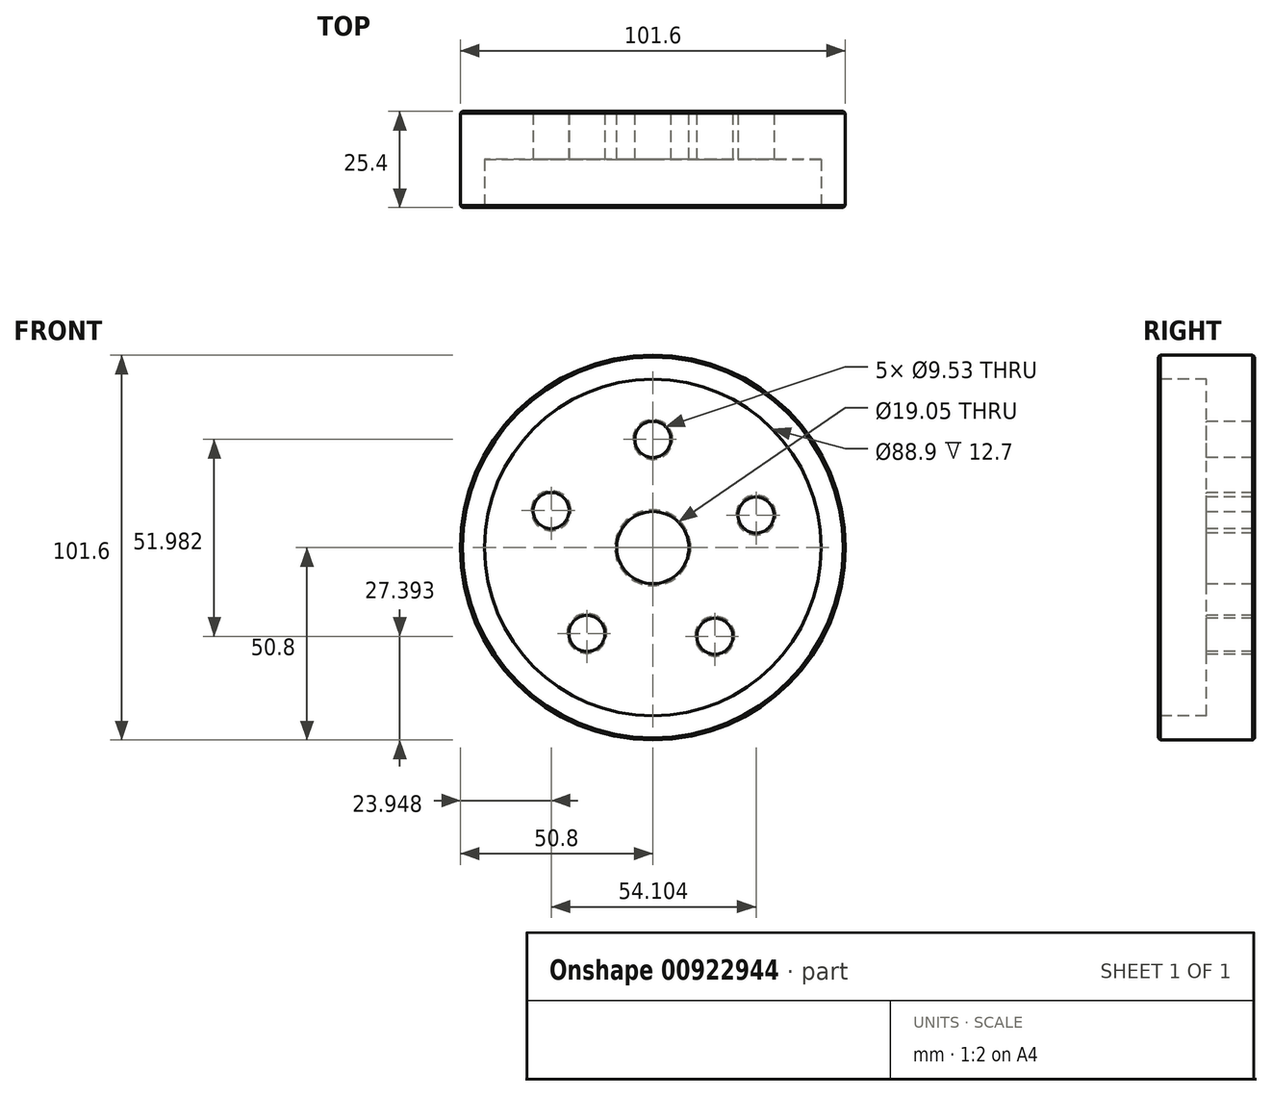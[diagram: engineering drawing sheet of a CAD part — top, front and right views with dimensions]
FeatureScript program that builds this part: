
annotation { "Feature Type Name" : "Feature", "Feature Type Description" : "" }
export const myFeature = defineFeature(function(context is Context, id is Id, definition is map)
    precondition{}
    {
        {
            var Q0;
            Q0=qCreatedBy(makeId("Front.planeOp"),FACE);
            var sketch = newSketch(context, id + "F0", { "sketchPlane" : qUnion([Q0])});
            skCircle(sketch, "E0", {"center": v(0, 0) * mm, "radius": 50.8 * mm});
            skCircle(sketch, "E1", {"center": v(0, 0) * mm, "radius": 9.53 * mm});
            skSolve(sketch);
        }
        {
            var Q0;
            Q0=makeQuery(id+"F0.imprint","IMPRINT",FACE,{"disambiguationData":[TD([[makeQuery(id+"F0.imprint","IMPRINT",EDGE,{"derivedFrom":sQuery(id+"F0.wireOp",EDGE,"E0")}),1.0]])]});
            extrude(context, id + "F1", {"entities" : qUnion([Q0]), "depth" : 25.4 * mm, "offsetDistance" : 25.4 * mm});
        }
        {
            var Q0;
            Q0=makeQuery(id+"F1.opExtrude","CAP_FACE",FACE,{"disambiguationData":[OSD([sQuery(id+"F0.wireOp",EDGE,"E0"),sQuery(id+"F0.wireOp",EDGE,"E1")])],"isStart":false});
            var sketch = newSketch(context, id + "F2", { "sketchPlane" : qUnion([Q0])});
            skCircle(sketch, "E2", {"center": v(0, 0) * mm, "radius": 44.45 * mm});
            skSolve(sketch);
        }
        {
            var Q0;
            Q0=makeQuery(id+"F2.imprint","IMPRINT",FACE,{"disambiguationData":[TD([[makeQuery(id+"F2.imprint","IMPRINT",EDGE,{"derivedFrom":sQuery(id+"F2.wireOp",EDGE,"E2")}),1.0]])]});
            extrude(context, id + "F3", {"entities" : qUnion([Q0]), "operationType" : NewBodyOperationType.REMOVE, "oppositeDirection" : true, "depth" : 12.7 * mm, "offsetDistance" : 25.4 * mm});
        }
        {
            var Q0;
            Q0=makeQuery(id+"F3.boolean.opBoolean","COPY",FACE,{"derivedFrom":makeQuery(id+"F3.opExtrude","CAP_FACE",FACE,{"disambiguationData":[OSD([sQuery(id+"F0.wireOp",EDGE,"E1"),sQuery(id+"F2.wireOp",EDGE,"E2")])],"isStart":false})});
            var sketch = newSketch(context, id + "F4", { "sketchPlane" : qUnion([Q0])});
            skCircle(sketch, "E3", {"center": v(0, 28.58) * mm, "radius": 4.76 * mm});
            skCircle(sketch, "E4.1.0", {"center": v(27.25, 8.6) * mm, "radius": 4.76 * mm});
            skCircle(sketch, "E4.2.0", {"center": v(16.39, -23.4) * mm, "radius": 4.76 * mm});
            skCircle(sketch, "E4.3.0", {"center": v(-17.4, -22.67) * mm, "radius": 4.76 * mm});
            skCircle(sketch, "E4.4.0", {"center": v(-26.85, 9.77) * mm, "radius": 4.76 * mm});
            skPoint(sketch, "E4.center", {"position": v(0, 0) * mm});
            skLineSegment(sketch, "E4.anchor1", {"start": v(0, 0) * mm, "end": v(0, 28.58) * mm, "construction": true});
            skLineSegment(sketch, "E4.anchor2", {"start": v(0, 0) * mm, "end": v(-26.85, 9.77) * mm, "construction": true});
            skSolve(sketch);
        }
        {
            var Q0;
            Q0=makeQuery(id+"F4.imprint","IMPRINT",FACE,{"disambiguationData":[TD([[makeQuery(id+"F4.imprint","IMPRINT",EDGE,{"derivedFrom":sQuery(id+"F4.wireOp",EDGE,"E4.4.0")}),1.0]])]});
            var Q1;
            Q1=makeQuery(id+"F4.imprint","IMPRINT",FACE,{"disambiguationData":[TD([[makeQuery(id+"F4.imprint","IMPRINT",EDGE,{"derivedFrom":sQuery(id+"F4.wireOp",EDGE,"E3")}),1.0]])]});
            var Q2;
            Q2=makeQuery(id+"F4.imprint","IMPRINT",FACE,{"disambiguationData":[TD([[makeQuery(id+"F4.imprint","IMPRINT",EDGE,{"derivedFrom":sQuery(id+"F4.wireOp",EDGE,"E4.1.0")}),1.0]])]});
            var Q3;
            Q3=makeQuery(id+"F4.imprint","IMPRINT",FACE,{"disambiguationData":[TD([[makeQuery(id+"F4.imprint","IMPRINT",EDGE,{"derivedFrom":sQuery(id+"F4.wireOp",EDGE,"E4.2.0")}),1.0]])]});
            var Q4;
            Q4=makeQuery(id+"F4.imprint","IMPRINT",FACE,{"disambiguationData":[TD([[makeQuery(id+"F4.imprint","IMPRINT",EDGE,{"derivedFrom":sQuery(id+"F4.wireOp",EDGE,"E4.3.0")}),1.0]])]});
            extrude(context, id + "F5", {"entities" : qUnion([Q0, Q1, Q2, Q3, Q4]), "operationType" : NewBodyOperationType.REMOVE, "endBound" : BoundingType.THROUGH_ALL, "oppositeDirection" : true, "depth" : 25.4 * mm, "offsetDistance" : 25.4 * mm});
        }
        {
            var Q0;
            Q0=makeQuery(id+"F3.boolean.opBoolean","COPY",EDGE,{"derivedFrom":makeQuery(id+"F3.opExtrude","CAP_EDGE",EDGE,{"disambiguationData":[OSD([sQuery(id+"F2.wireOp",EDGE,"E2")])],"isStart":true})});
            var Q1;
            Q1=makeQuery(id+"F5.boolean.opBoolean","COPY",EDGE,{"derivedFrom":makeQuery(id+"F5.opExtrude","CAP_EDGE",EDGE,{"disambiguationData":[OSD([sQuery(id+"F4.wireOp",EDGE,"E3")])],"isStart":true})});
            var Q2;
            Q2=makeQuery(id+"F5.boolean.opBoolean","COPY",EDGE,{"derivedFrom":makeQuery(id+"F5.opExtrude","CAP_EDGE",EDGE,{"disambiguationData":[OSD([sQuery(id+"F4.wireOp",EDGE,"E4.4.0")])],"isStart":true})});
            var Q3;
            Q3=makeQuery(id+"F3.boolean.opBoolean","COPY",EDGE,{"derivedFrom":makeQuery(id+"F3.opExtrude","CAP_EDGE",EDGE,{"disambiguationData":[OSD([sQuery(id+"F0.wireOp",EDGE,"E1")])],"isStart":false})});
            var Q4;
            Q4=makeQuery(id+"F5.boolean.opBoolean","COPY",EDGE,{"derivedFrom":makeQuery(id+"F5.opExtrude","CAP_EDGE",EDGE,{"disambiguationData":[OSD([sQuery(id+"F4.wireOp",EDGE,"E4.3.0")])],"isStart":true})});
            var Q5;
            Q5=makeQuery(id+"F1.opExtrude","CAP_EDGE",EDGE,{"disambiguationData":[OSD([sQuery(id+"F0.wireOp",EDGE,"E0")])],"isStart":true});
            var Q6;
            Q6=makeQuery(id+"F5.boolean.opBoolean","COPY",EDGE,{"derivedFrom":makeQuery(id+"F5.opExtrude","CAP_EDGE",EDGE,{"disambiguationData":[OSD([sQuery(id+"F4.wireOp",EDGE,"E4.2.0")])],"isStart":true})});
            var Q7;
            Q7=makeQuery(id+"F5.boolean.opBoolean","COPY",EDGE,{"derivedFrom":makeQuery(id+"F5.opExtrude","CAP_EDGE",EDGE,{"disambiguationData":[OSD([sQuery(id+"F4.wireOp",EDGE,"E4.1.0")])],"isStart":true})});
            var Q8;
            Q8=makeQuery(id+"F1.opExtrude","CAP_EDGE",EDGE,{"disambiguationData":[OSD([sQuery(id+"F0.wireOp",EDGE,"E0")])],"isStart":false});
            var Q9;
            Q9=makeQuery(id+"F5.boolean.opBoolean","INTERSECT",EDGE,{"derivedFrom":[makeQuery(id+"F1.opExtrude","CAP_FACE",FACE,{"disambiguationData":[OSD([sQuery(id+"F0.wireOp",EDGE,"E0"),sQuery(id+"F0.wireOp",EDGE,"E1")])],"isStart":true}),makeQuery(id+"F5.opExtrude","SWEPT_FACE",FACE,{"disambiguationData":[OSD([sQuery(id+"F4.wireOp",EDGE,"E3")])]})]});
            var Q10;
            Q10=makeQuery(id+"F5.boolean.opBoolean","INTERSECT",EDGE,{"derivedFrom":[makeQuery(id+"F1.opExtrude","CAP_FACE",FACE,{"disambiguationData":[OSD([sQuery(id+"F0.wireOp",EDGE,"E0"),sQuery(id+"F0.wireOp",EDGE,"E1")])],"isStart":true}),makeQuery(id+"F5.opExtrude","SWEPT_FACE",FACE,{"disambiguationData":[OSD([sQuery(id+"F4.wireOp",EDGE,"E4.4.0")])]})]});
            var Q11;
            Q11=makeQuery(id+"F5.boolean.opBoolean","INTERSECT",EDGE,{"derivedFrom":[makeQuery(id+"F1.opExtrude","CAP_FACE",FACE,{"disambiguationData":[OSD([sQuery(id+"F0.wireOp",EDGE,"E0"),sQuery(id+"F0.wireOp",EDGE,"E1")])],"isStart":true}),makeQuery(id+"F5.opExtrude","SWEPT_FACE",FACE,{"disambiguationData":[OSD([sQuery(id+"F4.wireOp",EDGE,"E4.3.0")])]})]});
            var Q12;
            Q12=makeQuery(id+"F5.boolean.opBoolean","INTERSECT",EDGE,{"derivedFrom":[makeQuery(id+"F1.opExtrude","CAP_FACE",FACE,{"disambiguationData":[OSD([sQuery(id+"F0.wireOp",EDGE,"E0"),sQuery(id+"F0.wireOp",EDGE,"E1")])],"isStart":true}),makeQuery(id+"F5.opExtrude","SWEPT_FACE",FACE,{"disambiguationData":[OSD([sQuery(id+"F4.wireOp",EDGE,"E4.2.0")])]})]});
            var Q13;
            Q13=makeQuery(id+"F5.boolean.opBoolean","INTERSECT",EDGE,{"derivedFrom":[makeQuery(id+"F1.opExtrude","CAP_FACE",FACE,{"disambiguationData":[OSD([sQuery(id+"F0.wireOp",EDGE,"E0"),sQuery(id+"F0.wireOp",EDGE,"E1")])],"isStart":true}),makeQuery(id+"F5.opExtrude","SWEPT_FACE",FACE,{"disambiguationData":[OSD([sQuery(id+"F4.wireOp",EDGE,"E4.1.0")])]})]});
            var Q14;
            Q14=makeQuery(id+"F1.opExtrude","CAP_EDGE",EDGE,{"disambiguationData":[OSD([sQuery(id+"F0.wireOp",EDGE,"E1")])],"isStart":true});
            chamfer(context, id + "F6", {"entities" : qUnion([Q0, Q1, Q2, Q3, Q4, Q5, Q6, Q7, Q8, Q9, Q10, Q11, Q12, Q13, Q14]), "width" : 0.5 * mm, "tangentPropagation" : true});
        }
    });
